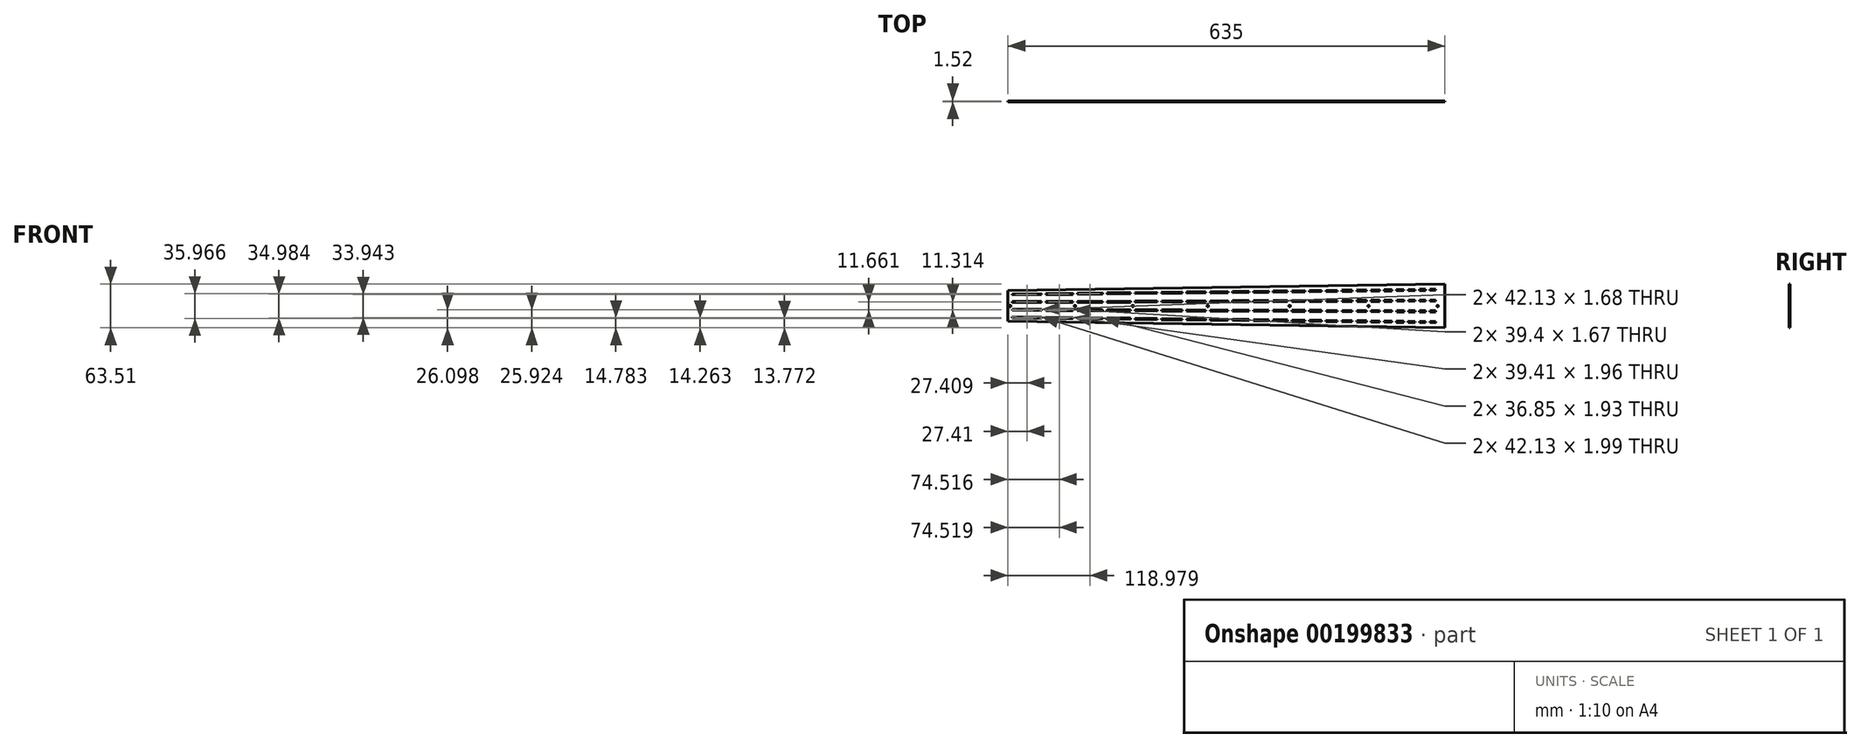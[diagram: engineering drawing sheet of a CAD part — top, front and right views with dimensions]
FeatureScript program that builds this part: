
annotation { "Feature Type Name" : "Feature", "Feature Type Description" : "" }
export const myFeature = defineFeature(function(context is Context, id is Id, definition is map)
    precondition{}
    {
        {
            var Q0;
            Q0=qCreatedBy(makeId("Front.planeOp"),FACE);
            var sketch = newSketch(context, id + "F0", { "sketchPlane" : qUnion([Q0])});
            skLineSegment(sketch, "E0", {"start": v(0, 5.56) * mm, "end": v(646.62, -1.59) * mm, "construction": true});
            skLineSegment(sketch, "E1", {"start": v(0, 6.32) * mm, "end": v(642.95, -0.78) * mm, "construction": true});
            skLineSegment(sketch, "E2", {"start": v(6.35, 5.49) * mm, "end": v(6.36, 6.25) * mm});
            skLineSegment(sketch, "E3", {"start": v(6.36, 6.25) * mm, "end": v(48.48, 5.78) * mm});
            skLineSegment(sketch, "E4", {"start": v(48.48, 5.78) * mm, "end": v(48.47, 5.02) * mm});
            skLineSegment(sketch, "E5", {"start": v(54.82, 4.95) * mm, "end": v(54.83, 5.71) * mm});
            skLineSegment(sketch, "E6", {"start": v(54.83, 5.71) * mm, "end": v(94.22, 5.28) * mm});
            skLineSegment(sketch, "E7", {"start": v(94.22, 5.28) * mm, "end": v(94.21, 4.52) * mm});
            skLineSegment(sketch, "E8", {"start": v(100.56, 4.45) * mm, "end": v(100.57, 5.2) * mm});
            skLineSegment(sketch, "E9", {"start": v(100.57, 5.2) * mm, "end": v(137.4, 4.8) * mm});
            skLineSegment(sketch, "E10", {"start": v(137.4, 4.8) * mm, "end": v(137.4, 4.04) * mm});
            skLineSegment(sketch, "E11", {"start": v(143.74, 3.97) * mm, "end": v(143.75, 4.73) * mm});
            skLineSegment(sketch, "E12", {"start": v(143.75, 4.73) * mm, "end": v(178.15, 4.35) * mm});
            skLineSegment(sketch, "E13", {"start": v(178.15, 4.35) * mm, "end": v(178.14, 3.59) * mm});
            skLineSegment(sketch, "E14", {"start": v(184.5, 3.52) * mm, "end": v(184.5, 4.28) * mm});
            skLineSegment(sketch, "E15", {"start": v(184.5, 4.28) * mm, "end": v(216.63, 3.93) * mm, "construction": true});
            skLineSegment(sketch, "E16", {"start": v(216.63, 3.93) * mm, "end": v(216.62, 3.16) * mm});
            skLineSegment(sketch, "E17", {"start": v(222.97, 3.1) * mm, "end": v(222.98, 3.85) * mm});
            skLineSegment(sketch, "E18", {"start": v(222.98, 3.85) * mm, "end": v(252.94, 3.52) * mm});
            skLineSegment(sketch, "E19", {"start": v(252.94, 3.52) * mm, "end": v(252.93, 2.76) * mm});
            skLineSegment(sketch, "E20", {"start": v(259.28, 2.7) * mm, "end": v(259.28, 3.45) * mm});
            skLineSegment(sketch, "E21", {"start": v(259.28, 3.45) * mm, "end": v(287.2, 3.15) * mm});
            skLineSegment(sketch, "E22", {"start": v(287.2, 3.15) * mm, "end": v(287.2, 2.38) * mm});
            skLineSegment(sketch, "E23", {"start": v(293.55, 2.31) * mm, "end": v(293.56, 3.08) * mm});
            skLineSegment(sketch, "E24", {"start": v(293.56, 3.08) * mm, "end": v(319.55, 2.79) * mm});
            skLineSegment(sketch, "E25", {"start": v(319.55, 2.79) * mm, "end": v(319.55, 2.03) * mm});
            skLineSegment(sketch, "E26", {"start": v(325.9, 1.96) * mm, "end": v(325.9, 2.72) * mm});
            skLineSegment(sketch, "E27", {"start": v(325.9, 2.72) * mm, "end": v(350.09, 2.45) * mm});
            skLineSegment(sketch, "E28", {"start": v(350.09, 2.45) * mm, "end": v(350.08, 1.69) * mm});
            skLineSegment(sketch, "E29", {"start": v(184.5, 4.28) * mm, "end": v(216.63, 3.93) * mm});
            skLineSegment(sketch, "E30", {"start": v(356.43, 1.62) * mm, "end": v(356.44, 2.38) * mm});
            skLineSegment(sketch, "E31", {"start": v(356.44, 2.38) * mm, "end": v(378.9, 2.13) * mm});
            skLineSegment(sketch, "E32", {"start": v(378.9, 2.13) * mm, "end": v(378.9, 1.37) * mm});
            skLineSegment(sketch, "E33", {"start": v(385.25, 1.3) * mm, "end": v(385.26, 2.06) * mm});
            skLineSegment(sketch, "E34", {"start": v(385.26, 2.06) * mm, "end": v(406.1, 1.83) * mm});
            skLineSegment(sketch, "E35", {"start": v(406.1, 1.83) * mm, "end": v(406.1, 1.07) * mm});
            skLineSegment(sketch, "E36", {"start": v(412.45, 1) * mm, "end": v(412.46, 1.76) * mm});
            skLineSegment(sketch, "E37", {"start": v(412.46, 1.76) * mm, "end": v(431.78, 1.55) * mm});
            skLineSegment(sketch, "E38", {"start": v(431.78, 1.55) * mm, "end": v(431.77, 0.79) * mm});
            skLineSegment(sketch, "E39", {"start": v(438.12, 0.72) * mm, "end": v(438.13, 1.48) * mm});
            skLineSegment(sketch, "E40", {"start": v(438.13, 1.48) * mm, "end": v(456.02, 1.28) * mm});
            skLineSegment(sketch, "E41", {"start": v(456.02, 1.28) * mm, "end": v(456, 0.52) * mm});
            skLineSegment(sketch, "E42", {"start": v(462.36, 0.45) * mm, "end": v(462.37, 1.21) * mm});
            skLineSegment(sketch, "E43", {"start": v(462.37, 1.21) * mm, "end": v(478.89, 1.03) * mm});
            skLineSegment(sketch, "E44", {"start": v(478.89, 1.03) * mm, "end": v(478.88, 0.27) * mm});
            skLineSegment(sketch, "E45", {"start": v(485.23, 0.2) * mm, "end": v(485.24, 0.96) * mm});
            skLineSegment(sketch, "E46", {"start": v(485.24, 0.96) * mm, "end": v(500.48, 0.79) * mm});
            skLineSegment(sketch, "E47", {"start": v(500.48, 0.79) * mm, "end": v(500.47, 0.03) * mm});
            skLineSegment(sketch, "E48", {"start": v(506.82, -0.04) * mm, "end": v(506.83, 0.72) * mm});
            skLineSegment(sketch, "E49", {"start": v(506.83, 0.72) * mm, "end": v(520.86, 0.56) * mm});
            skLineSegment(sketch, "E50", {"start": v(520.86, 0.56) * mm, "end": v(520.85, -0.2) * mm});
            skLineSegment(sketch, "E51", {"start": v(527.2, -0.27) * mm, "end": v(527.2, 0.5) * mm});
            skLineSegment(sketch, "E52", {"start": v(527.2, 0.5) * mm, "end": v(540.1, 0.35) * mm});
            skLineSegment(sketch, "E53", {"start": v(540.1, 0.35) * mm, "end": v(540.08, -0.41) * mm});
            skLineSegment(sketch, "E54", {"start": v(546.43, -0.48) * mm, "end": v(546.44, 0.28) * mm});
            skLineSegment(sketch, "E55", {"start": v(546.44, 0.28) * mm, "end": v(558.25, 0.15) * mm});
            skLineSegment(sketch, "E56", {"start": v(558.25, 0.15) * mm, "end": v(558.24, -0.61) * mm});
            skLineSegment(sketch, "E57", {"start": v(564.59, -0.68) * mm, "end": v(564.6, 0.08) * mm});
            skLineSegment(sketch, "E58", {"start": v(564.6, 0.08) * mm, "end": v(575.38, -0.04) * mm});
            skLineSegment(sketch, "E59", {"start": v(575.38, -0.04) * mm, "end": v(575.37, -0.8) * mm});
            skLineSegment(sketch, "E60", {"start": v(581.72, -0.87) * mm, "end": v(581.73, -0.1) * mm});
            skLineSegment(sketch, "E61", {"start": v(581.73, -0.1) * mm, "end": v(591.56, -0.22) * mm});
            skLineSegment(sketch, "E62", {"start": v(591.56, -0.22) * mm, "end": v(591.55, -0.98) * mm});
            skLineSegment(sketch, "E63", {"start": v(597.9, -1.05) * mm, "end": v(597.9, -0.29) * mm});
            skLineSegment(sketch, "E64", {"start": v(597.9, -0.29) * mm, "end": v(606.82, -0.39) * mm});
            skLineSegment(sketch, "E65", {"start": v(606.82, -0.39) * mm, "end": v(606.81, -1.15) * mm});
            skLineSegment(sketch, "E66", {"start": v(613.16, -1.22) * mm, "end": v(613.17, -0.46) * mm});
            skLineSegment(sketch, "E67", {"start": v(613.17, -0.46) * mm, "end": v(621.23, -0.54) * mm});
            skLineSegment(sketch, "E68", {"start": v(621.23, -0.54) * mm, "end": v(621.22, -1.3) * mm});
            skLineSegment(sketch, "E69.MirrorCS", {"start": v(184.5, 3.52) * mm, "end": v(184.48, 2.76) * mm});
            skLineSegment(sketch, "E70.MirrorCS", {"start": v(606.8, -1.9) * mm, "end": v(606.81, -1.15) * mm});
            skLineSegment(sketch, "E71.MirrorCS", {"start": v(222.97, 3.1) * mm, "end": v(222.96, 2.33) * mm});
            skLineSegment(sketch, "E72.MirrorCS", {"start": v(558.23, -1.37) * mm, "end": v(558.24, -0.61) * mm});
            skLineSegment(sketch, "E73.MirrorCS", {"start": v(216.6, 2.4) * mm, "end": v(216.62, 3.16) * mm});
            skLineSegment(sketch, "E74.MirrorCS", {"start": v(293.55, 2.31) * mm, "end": v(293.54, 1.55) * mm});
            skLineSegment(sketch, "E75.MirrorCS", {"start": v(94.2, 3.75) * mm, "end": v(94.21, 4.52) * mm});
            skLineSegment(sketch, "E76.MirrorCS", {"start": v(48.46, 4.26) * mm, "end": v(48.47, 5.02) * mm});
            skLineSegment(sketch, "E77.MirrorCS", {"start": v(613.16, -1.22) * mm, "end": v(613.15, -1.98) * mm});
            skLineSegment(sketch, "E78.MirrorCS", {"start": v(597.9, -1.05) * mm, "end": v(597.89, -1.81) * mm});
            skLineSegment(sketch, "E79.MirrorCS", {"start": v(325.9, 1.96) * mm, "end": v(325.89, 1.2) * mm});
            skLineSegment(sketch, "E80.MirrorCS", {"start": v(581.72, -0.87) * mm, "end": v(581.71, -1.63) * mm});
            skLineSegment(sketch, "E81.MirrorCS", {"start": v(478.87, -0.5) * mm, "end": v(478.88, 0.27) * mm});
            skLineSegment(sketch, "E82.MirrorCS", {"start": v(406.1, 0.3) * mm, "end": v(406.1, 1.07) * mm});
            skLineSegment(sketch, "E83.MirrorCS", {"start": v(591.54, -1.74) * mm, "end": v(591.55, -0.98) * mm});
            skLineSegment(sketch, "E84.MirrorCS", {"start": v(485.23, 0.2) * mm, "end": v(485.22, -0.57) * mm});
            skLineSegment(sketch, "E85.MirrorCS", {"start": v(581.71, -1.63) * mm, "end": v(591.54, -1.74) * mm});
            skLineSegment(sketch, "E86.MirrorCS", {"start": v(520.84, -0.96) * mm, "end": v(520.85, -0.2) * mm});
            skLineSegment(sketch, "E87.MirrorCS", {"start": v(319.54, 1.26) * mm, "end": v(319.55, 2.03) * mm});
            skLineSegment(sketch, "E88.MirrorCS", {"start": v(456, -0.24) * mm, "end": v(456, 0.52) * mm});
            skLineSegment(sketch, "E89.MirrorCS", {"start": v(564.59, -0.68) * mm, "end": v(564.58, -1.44) * mm});
            skLineSegment(sketch, "E90.MirrorCS", {"start": v(385.25, 1.3) * mm, "end": v(385.24, 0.54) * mm});
            skLineSegment(sketch, "E91.MirrorCS", {"start": v(378.89, 0.6) * mm, "end": v(378.9, 1.37) * mm});
            skLineSegment(sketch, "E92.MirrorCS", {"start": v(506.82, -0.04) * mm, "end": v(506.81, -0.8) * mm});
            skLineSegment(sketch, "E93.MirrorCS", {"start": v(597.89, -1.81) * mm, "end": v(606.8, -1.9) * mm});
            skLineSegment(sketch, "E94.MirrorCS", {"start": v(546.42, -1.24) * mm, "end": v(558.23, -1.37) * mm});
            skLineSegment(sketch, "E95.MirrorCS", {"start": v(143.74, 3.97) * mm, "end": v(143.74, 3.2) * mm});
            skLineSegment(sketch, "E96.MirrorCS", {"start": v(137.39, 3.28) * mm, "end": v(137.4, 4.04) * mm});
            skLineSegment(sketch, "E97.MirrorCS", {"start": v(100.56, 4.45) * mm, "end": v(100.56, 3.68) * mm});
            skLineSegment(sketch, "E98.MirrorCS", {"start": v(54.82, 4.95) * mm, "end": v(54.8, 4.19) * mm});
            skLineSegment(sketch, "E99.MirrorCS", {"start": v(6.35, 5.49) * mm, "end": v(6.34, 4.72) * mm});
            skLineSegment(sketch, "E100.MirrorCS", {"start": v(178.13, 2.83) * mm, "end": v(178.14, 3.59) * mm});
            skLineSegment(sketch, "E101.MirrorCS", {"start": v(431.77, 0.02) * mm, "end": v(431.77, 0.79) * mm});
            skLineSegment(sketch, "E102.MirrorCS", {"start": v(546.43, -0.48) * mm, "end": v(546.42, -1.24) * mm});
            skLineSegment(sketch, "E103.MirrorCS", {"start": v(500.46, -0.73) * mm, "end": v(500.47, 0.03) * mm});
            skLineSegment(sketch, "E104.MirrorCS", {"start": v(287.2, 1.62) * mm, "end": v(287.2, 2.38) * mm});
            skLineSegment(sketch, "E105.MirrorCS", {"start": v(564.58, -1.44) * mm, "end": v(575.36, -1.56) * mm});
            skLineSegment(sketch, "E106.MirrorCS", {"start": v(252.92, 2) * mm, "end": v(252.93, 2.76) * mm});
            skLineSegment(sketch, "E107.MirrorCS", {"start": v(613.15, -1.98) * mm, "end": v(621.21, -2.07) * mm});
            skLineSegment(sketch, "E108.MirrorCS", {"start": v(527.2, -0.27) * mm, "end": v(527.19, -1.03) * mm});
            skLineSegment(sketch, "E109.MirrorCS", {"start": v(350.07, 0.93) * mm, "end": v(350.08, 1.69) * mm});
            skLineSegment(sketch, "E110.MirrorCS", {"start": v(412.45, 1) * mm, "end": v(412.44, 0.24) * mm});
            skLineSegment(sketch, "E111.MirrorCS", {"start": v(575.36, -1.56) * mm, "end": v(575.37, -0.8) * mm});
            skLineSegment(sketch, "E112.MirrorCS", {"start": v(259.28, 2.7) * mm, "end": v(259.27, 1.93) * mm});
            skLineSegment(sketch, "E113.MirrorCS", {"start": v(621.21, -2.07) * mm, "end": v(621.22, -1.3) * mm});
            skLineSegment(sketch, "E114.MirrorCS", {"start": v(356.43, 1.62) * mm, "end": v(356.42, 0.86) * mm});
            skLineSegment(sketch, "E115.MirrorCS", {"start": v(506.81, -0.8) * mm, "end": v(520.84, -0.96) * mm});
            skLineSegment(sketch, "E116.MirrorCS", {"start": v(438.12, 0.72) * mm, "end": v(438.11, -0.05) * mm});
            skLineSegment(sketch, "E117.MirrorCS", {"start": v(184.48, 2.76) * mm, "end": v(216.6, 2.4) * mm, "construction": true});
            skLineSegment(sketch, "E118.MirrorCS", {"start": v(462.36, 0.45) * mm, "end": v(462.35, -0.31) * mm});
            skLineSegment(sketch, "E119.MirrorCS", {"start": v(540.07, -1.17) * mm, "end": v(540.08, -0.41) * mm});
            skLineSegment(sketch, "E120.MirrorCS", {"start": v(527.19, -1.03) * mm, "end": v(540.07, -1.17) * mm});
            skLineSegment(sketch, "E121.MirrorCS", {"start": v(222.96, 2.33) * mm, "end": v(252.92, 2) * mm});
            skLineSegment(sketch, "E122.MirrorCS", {"start": v(385.24, 0.54) * mm, "end": v(406.1, 0.3) * mm});
            skLineSegment(sketch, "E123.MirrorCS", {"start": v(293.54, 1.55) * mm, "end": v(319.54, 1.26) * mm});
            skLineSegment(sketch, "E124.MirrorCS", {"start": v(438.11, -0.05) * mm, "end": v(456, -0.24) * mm});
            skLineSegment(sketch, "E125.MirrorCS", {"start": v(143.74, 3.2) * mm, "end": v(178.13, 2.83) * mm});
            skLineSegment(sketch, "E126.MirrorCS", {"start": v(54.8, 4.19) * mm, "end": v(94.2, 3.75) * mm});
            skLineSegment(sketch, "E127.MirrorCS", {"start": v(6.34, 4.72) * mm, "end": v(48.46, 4.26) * mm});
            skLineSegment(sketch, "E128.MirrorCS", {"start": v(356.42, 0.86) * mm, "end": v(378.89, 0.6) * mm});
            skLineSegment(sketch, "E129.MirrorCS", {"start": v(259.27, 1.93) * mm, "end": v(287.2, 1.62) * mm});
            skLineSegment(sketch, "E130.MirrorCS", {"start": v(485.22, -0.57) * mm, "end": v(500.46, -0.73) * mm});
            skLineSegment(sketch, "E131.MirrorCS", {"start": v(412.44, 0.24) * mm, "end": v(431.77, 0.02) * mm});
            skLineSegment(sketch, "E132.MirrorCS", {"start": v(184.48, 2.76) * mm, "end": v(216.6, 2.4) * mm});
            skLineSegment(sketch, "E133.MirrorCS", {"start": v(462.35, -0.31) * mm, "end": v(478.87, -0.5) * mm});
            skLineSegment(sketch, "E134.MirrorCS", {"start": v(325.89, 1.2) * mm, "end": v(350.07, 0.93) * mm});
            skLineSegment(sketch, "E135.MirrorCS", {"start": v(100.56, 3.68) * mm, "end": v(137.39, 3.28) * mm});
            skLineSegment(sketch, "E136", {"start": v(-33.04, 0) * mm, "end": v(118.54, 0) * mm, "construction": true});
            skLineSegment(sketch, "E137", {"start": v(0, 16.67) * mm, "end": v(646.66, 14.29) * mm, "construction": true});
            skLineSegment(sketch, "E138", {"start": v(0, 17.43) * mm, "end": v(642.97, 15.06) * mm, "construction": true});
            skLineSegment(sketch, "E139", {"start": v(6.35, 16.65) * mm, "end": v(6.35, 17.4) * mm});
            skLineSegment(sketch, "E140", {"start": v(6.35, 17.4) * mm, "end": v(48.47, 17.25) * mm});
            skLineSegment(sketch, "E141", {"start": v(48.47, 17.25) * mm, "end": v(48.47, 16.5) * mm});
            skLineSegment(sketch, "E142", {"start": v(54.82, 16.47) * mm, "end": v(54.82, 17.23) * mm});
            skLineSegment(sketch, "E143", {"start": v(54.82, 17.23) * mm, "end": v(94.22, 17.08) * mm});
            skLineSegment(sketch, "E144", {"start": v(94.22, 17.08) * mm, "end": v(94.22, 16.32) * mm});
            skLineSegment(sketch, "E145", {"start": v(100.57, 16.3) * mm, "end": v(100.57, 17.06) * mm});
            skLineSegment(sketch, "E146", {"start": v(100.57, 17.06) * mm, "end": v(137.4, 16.92) * mm});
            skLineSegment(sketch, "E147", {"start": v(137.4, 16.92) * mm, "end": v(137.4, 16.16) * mm});
            skLineSegment(sketch, "E148", {"start": v(143.75, 16.14) * mm, "end": v(143.75, 16.9) * mm});
            skLineSegment(sketch, "E149", {"start": v(143.75, 16.9) * mm, "end": v(178.15, 16.77) * mm});
            skLineSegment(sketch, "E150", {"start": v(178.15, 16.77) * mm, "end": v(178.15, 16.01) * mm});
            skLineSegment(sketch, "E151", {"start": v(184.5, 15.99) * mm, "end": v(184.5, 16.75) * mm});
            skLineSegment(sketch, "E152", {"start": v(184.5, 16.75) * mm, "end": v(216.63, 16.63) * mm, "construction": true});
            skLineSegment(sketch, "E153", {"start": v(216.63, 16.63) * mm, "end": v(216.63, 15.87) * mm});
            skLineSegment(sketch, "E154", {"start": v(222.98, 15.85) * mm, "end": v(222.98, 16.6) * mm});
            skLineSegment(sketch, "E155", {"start": v(222.98, 16.6) * mm, "end": v(252.94, 16.5) * mm});
            skLineSegment(sketch, "E156", {"start": v(252.94, 16.5) * mm, "end": v(252.94, 15.74) * mm});
            skLineSegment(sketch, "E157", {"start": v(259.3, 15.71) * mm, "end": v(259.3, 16.48) * mm});
            skLineSegment(sketch, "E158", {"start": v(259.3, 16.48) * mm, "end": v(287.22, 16.37) * mm});
            skLineSegment(sketch, "E159", {"start": v(287.22, 16.37) * mm, "end": v(287.21, 15.61) * mm});
            skLineSegment(sketch, "E160", {"start": v(293.56, 15.59) * mm, "end": v(293.57, 16.35) * mm});
            skLineSegment(sketch, "E161", {"start": v(293.57, 16.35) * mm, "end": v(319.57, 16.25) * mm});
            skLineSegment(sketch, "E162", {"start": v(319.57, 16.25) * mm, "end": v(319.56, 15.5) * mm});
            skLineSegment(sketch, "E163", {"start": v(325.91, 15.47) * mm, "end": v(325.92, 16.23) * mm});
            skLineSegment(sketch, "E164", {"start": v(325.92, 16.23) * mm, "end": v(350.1, 16.14) * mm});
            skLineSegment(sketch, "E165", {"start": v(350.1, 16.14) * mm, "end": v(350.1, 15.38) * mm});
            skLineSegment(sketch, "E166", {"start": v(184.5, 16.75) * mm, "end": v(216.63, 16.63) * mm});
            skLineSegment(sketch, "E167", {"start": v(356.45, 15.36) * mm, "end": v(356.45, 16.12) * mm});
            skLineSegment(sketch, "E168", {"start": v(356.45, 16.12) * mm, "end": v(378.92, 16.04) * mm});
            skLineSegment(sketch, "E169", {"start": v(378.92, 16.04) * mm, "end": v(378.92, 15.27) * mm});
            skLineSegment(sketch, "E170", {"start": v(385.27, 15.25) * mm, "end": v(385.27, 16.01) * mm});
            skLineSegment(sketch, "E171", {"start": v(385.27, 16.01) * mm, "end": v(406.12, 15.94) * mm});
            skLineSegment(sketch, "E172", {"start": v(406.12, 15.94) * mm, "end": v(406.12, 15.17) * mm});
            skLineSegment(sketch, "E173", {"start": v(412.47, 15.15) * mm, "end": v(412.47, 15.91) * mm});
            skLineSegment(sketch, "E174", {"start": v(412.47, 15.91) * mm, "end": v(431.8, 15.84) * mm});
            skLineSegment(sketch, "E175", {"start": v(431.8, 15.84) * mm, "end": v(431.8, 15.08) * mm});
            skLineSegment(sketch, "E176", {"start": v(438.15, 15.06) * mm, "end": v(438.15, 15.82) * mm});
            skLineSegment(sketch, "E177", {"start": v(438.15, 15.82) * mm, "end": v(456.03, 15.75) * mm});
            skLineSegment(sketch, "E178", {"start": v(456.03, 15.75) * mm, "end": v(456.03, 14.99) * mm});
            skLineSegment(sketch, "E179", {"start": v(462.38, 14.97) * mm, "end": v(462.38, 15.73) * mm});
            skLineSegment(sketch, "E180", {"start": v(462.38, 15.73) * mm, "end": v(478.9, 15.67) * mm});
            skLineSegment(sketch, "E181", {"start": v(478.9, 15.67) * mm, "end": v(478.9, 14.9) * mm});
            skLineSegment(sketch, "E182", {"start": v(485.26, 14.88) * mm, "end": v(485.26, 15.64) * mm});
            skLineSegment(sketch, "E183", {"start": v(485.26, 15.64) * mm, "end": v(500.5, 15.59) * mm});
            skLineSegment(sketch, "E184", {"start": v(500.5, 15.59) * mm, "end": v(500.5, 14.83) * mm});
            skLineSegment(sketch, "E185", {"start": v(506.85, 14.8) * mm, "end": v(506.85, 15.56) * mm});
            skLineSegment(sketch, "E186", {"start": v(506.85, 15.56) * mm, "end": v(520.88, 15.51) * mm});
            skLineSegment(sketch, "E187", {"start": v(520.88, 15.51) * mm, "end": v(520.88, 14.75) * mm});
            skLineSegment(sketch, "E188", {"start": v(527.23, 14.73) * mm, "end": v(527.23, 15.49) * mm});
            skLineSegment(sketch, "E189", {"start": v(527.23, 15.49) * mm, "end": v(540.11, 15.44) * mm});
            skLineSegment(sketch, "E190", {"start": v(540.11, 15.44) * mm, "end": v(540.11, 14.68) * mm});
            skLineSegment(sketch, "E191", {"start": v(546.46, 14.66) * mm, "end": v(546.46, 15.42) * mm});
            skLineSegment(sketch, "E192", {"start": v(546.46, 15.42) * mm, "end": v(558.27, 15.37) * mm});
            skLineSegment(sketch, "E193", {"start": v(558.27, 15.37) * mm, "end": v(558.27, 14.61) * mm});
            skLineSegment(sketch, "E194", {"start": v(564.62, 14.59) * mm, "end": v(564.62, 15.35) * mm});
            skLineSegment(sketch, "E195", {"start": v(564.62, 15.35) * mm, "end": v(575.4, 15.31) * mm});
            skLineSegment(sketch, "E196", {"start": v(575.4, 15.31) * mm, "end": v(575.4, 14.55) * mm});
            skLineSegment(sketch, "E197", {"start": v(581.75, 14.53) * mm, "end": v(581.76, 15.29) * mm});
            skLineSegment(sketch, "E198", {"start": v(581.76, 15.29) * mm, "end": v(591.58, 15.25) * mm});
            skLineSegment(sketch, "E199", {"start": v(591.58, 15.25) * mm, "end": v(591.58, 14.5) * mm});
            skLineSegment(sketch, "E200", {"start": v(597.93, 14.47) * mm, "end": v(597.93, 15.23) * mm});
            skLineSegment(sketch, "E201", {"start": v(597.93, 15.23) * mm, "end": v(606.85, 15.2) * mm});
            skLineSegment(sketch, "E202", {"start": v(606.85, 15.2) * mm, "end": v(606.85, 14.43) * mm});
            skLineSegment(sketch, "E203", {"start": v(613.2, 14.41) * mm, "end": v(613.2, 15.17) * mm});
            skLineSegment(sketch, "E204", {"start": v(613.2, 15.17) * mm, "end": v(621.26, 15.14) * mm});
            skLineSegment(sketch, "E205", {"start": v(621.26, 15.14) * mm, "end": v(621.26, 14.38) * mm});
            skLineSegment(sketch, "E206.MirrorCS", {"start": v(184.5, 15.99) * mm, "end": v(184.5, 15.23) * mm});
            skLineSegment(sketch, "E207.MirrorCS", {"start": v(606.84, 13.67) * mm, "end": v(606.85, 14.43) * mm});
            skLineSegment(sketch, "E208.MirrorCS", {"start": v(222.98, 15.85) * mm, "end": v(222.98, 15.09) * mm});
            skLineSegment(sketch, "E209.MirrorCS", {"start": v(558.27, 13.85) * mm, "end": v(558.27, 14.61) * mm});
            skLineSegment(sketch, "E210.MirrorCS", {"start": v(216.63, 15.1) * mm, "end": v(216.63, 15.87) * mm});
            skLineSegment(sketch, "E211.MirrorCS", {"start": v(293.56, 15.59) * mm, "end": v(293.56, 14.83) * mm});
            skLineSegment(sketch, "E212.MirrorCS", {"start": v(94.22, 15.56) * mm, "end": v(94.22, 16.32) * mm});
            skLineSegment(sketch, "E213.MirrorCS", {"start": v(48.47, 15.73) * mm, "end": v(48.47, 16.5) * mm});
            skLineSegment(sketch, "E214.MirrorCS", {"start": v(613.2, 14.41) * mm, "end": v(613.2, 13.65) * mm});
            skLineSegment(sketch, "E215.MirrorCS", {"start": v(597.93, 14.47) * mm, "end": v(597.93, 13.7) * mm});
            skLineSegment(sketch, "E216.MirrorCS", {"start": v(325.91, 15.47) * mm, "end": v(325.91, 14.7) * mm});
            skLineSegment(sketch, "E217.MirrorCS", {"start": v(581.75, 14.53) * mm, "end": v(581.75, 13.76) * mm});
            skLineSegment(sketch, "E218.MirrorCS", {"start": v(478.9, 14.14) * mm, "end": v(478.9, 14.9) * mm});
            skLineSegment(sketch, "E219.MirrorCS", {"start": v(406.12, 14.41) * mm, "end": v(406.12, 15.17) * mm});
            skLineSegment(sketch, "E220.MirrorCS", {"start": v(591.58, 13.73) * mm, "end": v(591.58, 14.5) * mm});
            skLineSegment(sketch, "E221.MirrorCS", {"start": v(485.26, 14.88) * mm, "end": v(485.25, 14.12) * mm});
            skLineSegment(sketch, "E222.MirrorCS", {"start": v(581.75, 13.76) * mm, "end": v(591.58, 13.73) * mm});
            skLineSegment(sketch, "E223.MirrorCS", {"start": v(520.87, 13.99) * mm, "end": v(520.88, 14.75) * mm});
            skLineSegment(sketch, "E224.MirrorCS", {"start": v(319.56, 14.73) * mm, "end": v(319.56, 15.5) * mm});
            skLineSegment(sketch, "E225.MirrorCS", {"start": v(456.03, 14.23) * mm, "end": v(456.03, 14.99) * mm});
            skLineSegment(sketch, "E226.MirrorCS", {"start": v(564.62, 14.59) * mm, "end": v(564.61, 13.83) * mm});
            skLineSegment(sketch, "E227.MirrorCS", {"start": v(385.27, 15.25) * mm, "end": v(385.27, 14.49) * mm});
            skLineSegment(sketch, "E228.MirrorCS", {"start": v(378.92, 14.51) * mm, "end": v(378.92, 15.27) * mm});
            skLineSegment(sketch, "E229.MirrorCS", {"start": v(506.85, 14.8) * mm, "end": v(506.84, 14.04) * mm});
            skLineSegment(sketch, "E230.MirrorCS", {"start": v(597.93, 13.7) * mm, "end": v(606.84, 13.67) * mm});
            skLineSegment(sketch, "E231.MirrorCS", {"start": v(546.46, 13.9) * mm, "end": v(558.27, 13.85) * mm});
            skLineSegment(sketch, "E232.MirrorCS", {"start": v(143.75, 16.14) * mm, "end": v(143.75, 15.38) * mm});
            skLineSegment(sketch, "E233.MirrorCS", {"start": v(137.4, 15.4) * mm, "end": v(137.4, 16.16) * mm});
            skLineSegment(sketch, "E234.MirrorCS", {"start": v(100.57, 16.3) * mm, "end": v(100.57, 15.54) * mm});
            skLineSegment(sketch, "E235.MirrorCS", {"start": v(54.82, 16.47) * mm, "end": v(54.82, 15.7) * mm});
            skLineSegment(sketch, "E236.MirrorCS", {"start": v(6.35, 16.65) * mm, "end": v(6.35, 15.88) * mm});
            skLineSegment(sketch, "E237.MirrorCS", {"start": v(178.15, 15.25) * mm, "end": v(178.15, 16.01) * mm});
            skLineSegment(sketch, "E238.MirrorCS", {"start": v(431.8, 14.32) * mm, "end": v(431.8, 15.08) * mm});
            skLineSegment(sketch, "E239.MirrorCS", {"start": v(546.46, 14.66) * mm, "end": v(546.46, 13.9) * mm});
            skLineSegment(sketch, "E240.MirrorCS", {"start": v(500.5, 14.06) * mm, "end": v(500.5, 14.83) * mm});
            skLineSegment(sketch, "E241.MirrorCS", {"start": v(287.21, 14.85) * mm, "end": v(287.21, 15.61) * mm});
            skLineSegment(sketch, "E242.MirrorCS", {"start": v(564.61, 13.83) * mm, "end": v(575.4, 13.79) * mm});
            skLineSegment(sketch, "E243.MirrorCS", {"start": v(252.94, 14.98) * mm, "end": v(252.94, 15.74) * mm});
            skLineSegment(sketch, "E244.MirrorCS", {"start": v(613.2, 13.65) * mm, "end": v(621.25, 13.62) * mm});
            skLineSegment(sketch, "E245.MirrorCS", {"start": v(527.23, 14.73) * mm, "end": v(527.22, 13.97) * mm});
            skLineSegment(sketch, "E246.MirrorCS", {"start": v(350.1, 14.62) * mm, "end": v(350.1, 15.38) * mm});
            skLineSegment(sketch, "E247.MirrorCS", {"start": v(412.47, 15.15) * mm, "end": v(412.47, 14.39) * mm});
            skLineSegment(sketch, "E248.MirrorCS", {"start": v(575.4, 13.79) * mm, "end": v(575.4, 14.55) * mm});
            skLineSegment(sketch, "E249.MirrorCS", {"start": v(259.3, 15.71) * mm, "end": v(259.29, 14.95) * mm});
            skLineSegment(sketch, "E250.MirrorCS", {"start": v(621.25, 13.62) * mm, "end": v(621.26, 14.38) * mm});
            skLineSegment(sketch, "E251.MirrorCS", {"start": v(356.45, 15.36) * mm, "end": v(356.44, 14.6) * mm});
            skLineSegment(sketch, "E252.MirrorCS", {"start": v(506.84, 14.04) * mm, "end": v(520.87, 13.99) * mm});
            skLineSegment(sketch, "E253.MirrorCS", {"start": v(438.15, 15.06) * mm, "end": v(438.14, 14.3) * mm});
            skLineSegment(sketch, "E254.MirrorCS", {"start": v(184.5, 15.23) * mm, "end": v(216.63, 15.1) * mm, "construction": true});
            skLineSegment(sketch, "E255.MirrorCS", {"start": v(462.38, 14.97) * mm, "end": v(462.38, 14.2) * mm});
            skLineSegment(sketch, "E256.MirrorCS", {"start": v(540.1, 13.92) * mm, "end": v(540.11, 14.68) * mm});
            skLineSegment(sketch, "E257.MirrorCS", {"start": v(527.22, 13.97) * mm, "end": v(540.1, 13.92) * mm});
            skLineSegment(sketch, "E258.MirrorCS", {"start": v(222.98, 15.09) * mm, "end": v(252.94, 14.98) * mm});
            skLineSegment(sketch, "E259.MirrorCS", {"start": v(385.27, 14.49) * mm, "end": v(406.12, 14.41) * mm});
            skLineSegment(sketch, "E260.MirrorCS", {"start": v(293.56, 14.83) * mm, "end": v(319.56, 14.73) * mm});
            skLineSegment(sketch, "E261.MirrorCS", {"start": v(438.14, 14.3) * mm, "end": v(456.03, 14.23) * mm});
            skLineSegment(sketch, "E262.MirrorCS", {"start": v(143.75, 15.38) * mm, "end": v(178.15, 15.25) * mm});
            skLineSegment(sketch, "E263.MirrorCS", {"start": v(54.82, 15.7) * mm, "end": v(94.22, 15.56) * mm});
            skLineSegment(sketch, "E264.MirrorCS", {"start": v(6.35, 15.88) * mm, "end": v(48.47, 15.73) * mm});
            skLineSegment(sketch, "E265.MirrorCS", {"start": v(356.44, 14.6) * mm, "end": v(378.92, 14.51) * mm});
            skLineSegment(sketch, "E266.MirrorCS", {"start": v(259.29, 14.95) * mm, "end": v(287.21, 14.85) * mm});
            skLineSegment(sketch, "E267.MirrorCS", {"start": v(485.25, 14.12) * mm, "end": v(500.5, 14.06) * mm});
            skLineSegment(sketch, "E268.MirrorCS", {"start": v(412.47, 14.39) * mm, "end": v(431.8, 14.32) * mm});
            skLineSegment(sketch, "E269.MirrorCS", {"start": v(184.5, 15.23) * mm, "end": v(216.63, 15.1) * mm});
            skLineSegment(sketch, "E270.MirrorCS", {"start": v(462.38, 14.2) * mm, "end": v(478.9, 14.14) * mm});
            skLineSegment(sketch, "E271.MirrorCS", {"start": v(325.91, 14.7) * mm, "end": v(350.1, 14.62) * mm});
            skLineSegment(sketch, "E272.MirrorCS", {"start": v(100.57, 15.54) * mm, "end": v(137.4, 15.4) * mm});
            skLineSegment(sketch, "E273", {"start": v(0, 27.78) * mm, "end": v(646.66, 30.16) * mm, "construction": true});
            skLineSegment(sketch, "E274", {"start": v(0, 28.54) * mm, "end": v(642.97, 30.91) * mm, "construction": true});
            skLineSegment(sketch, "E275", {"start": v(6.35, 27.8) * mm, "end": v(6.35, 28.57) * mm});
            skLineSegment(sketch, "E276", {"start": v(6.35, 28.57) * mm, "end": v(48.47, 28.72) * mm});
            skLineSegment(sketch, "E277", {"start": v(48.47, 28.72) * mm, "end": v(48.47, 27.96) * mm});
            skLineSegment(sketch, "E278", {"start": v(54.82, 27.98) * mm, "end": v(54.82, 28.75) * mm});
            skLineSegment(sketch, "E279", {"start": v(54.82, 28.75) * mm, "end": v(94.22, 28.9) * mm});
            skLineSegment(sketch, "E280", {"start": v(94.22, 28.9) * mm, "end": v(94.22, 28.13) * mm});
            skLineSegment(sketch, "E281", {"start": v(100.57, 28.15) * mm, "end": v(100.57, 28.91) * mm});
            skLineSegment(sketch, "E282", {"start": v(100.57, 28.91) * mm, "end": v(137.4, 29.05) * mm});
            skLineSegment(sketch, "E283", {"start": v(137.4, 29.05) * mm, "end": v(137.4, 28.29) * mm});
            skLineSegment(sketch, "E284", {"start": v(143.75, 28.31) * mm, "end": v(143.75, 29.07) * mm});
            skLineSegment(sketch, "E285", {"start": v(143.75, 29.07) * mm, "end": v(178.15, 29.2) * mm});
            skLineSegment(sketch, "E286", {"start": v(178.15, 29.2) * mm, "end": v(178.15, 28.44) * mm});
            skLineSegment(sketch, "E287", {"start": v(184.5, 28.46) * mm, "end": v(184.5, 29.22) * mm});
            skLineSegment(sketch, "E288", {"start": v(184.5, 29.22) * mm, "end": v(216.63, 29.34) * mm, "construction": true});
            skLineSegment(sketch, "E289", {"start": v(216.63, 29.34) * mm, "end": v(216.63, 28.58) * mm});
            skLineSegment(sketch, "E290", {"start": v(222.98, 28.6) * mm, "end": v(222.98, 29.36) * mm});
            skLineSegment(sketch, "E291", {"start": v(222.98, 29.36) * mm, "end": v(252.94, 29.47) * mm});
            skLineSegment(sketch, "E292", {"start": v(252.94, 29.47) * mm, "end": v(252.94, 28.71) * mm});
            skLineSegment(sketch, "E293", {"start": v(259.3, 28.74) * mm, "end": v(259.29, 29.5) * mm});
            skLineSegment(sketch, "E294", {"start": v(259.29, 29.5) * mm, "end": v(287.21, 29.6) * mm});
            skLineSegment(sketch, "E295", {"start": v(287.21, 29.6) * mm, "end": v(287.21, 28.84) * mm});
            skLineSegment(sketch, "E296", {"start": v(293.56, 28.86) * mm, "end": v(293.56, 29.62) * mm});
            skLineSegment(sketch, "E297", {"start": v(293.56, 29.62) * mm, "end": v(319.56, 29.72) * mm});
            skLineSegment(sketch, "E298", {"start": v(319.56, 29.72) * mm, "end": v(319.56, 28.96) * mm});
            skLineSegment(sketch, "E299", {"start": v(325.91, 28.98) * mm, "end": v(325.91, 29.74) * mm});
            skLineSegment(sketch, "E300", {"start": v(325.91, 29.74) * mm, "end": v(350.1, 29.83) * mm});
            skLineSegment(sketch, "E301", {"start": v(350.1, 29.83) * mm, "end": v(350.1, 29.07) * mm});
            skLineSegment(sketch, "E302", {"start": v(184.5, 29.22) * mm, "end": v(216.63, 29.34) * mm});
            skLineSegment(sketch, "E303", {"start": v(356.45, 29.1) * mm, "end": v(356.44, 29.86) * mm});
            skLineSegment(sketch, "E304", {"start": v(356.44, 29.86) * mm, "end": v(378.92, 29.94) * mm});
            skLineSegment(sketch, "E305", {"start": v(378.92, 29.94) * mm, "end": v(378.92, 29.18) * mm});
            skLineSegment(sketch, "E306", {"start": v(385.27, 29.2) * mm, "end": v(385.27, 29.96) * mm});
            skLineSegment(sketch, "E307", {"start": v(385.27, 29.96) * mm, "end": v(406.12, 30.04) * mm});
            skLineSegment(sketch, "E308", {"start": v(406.12, 30.04) * mm, "end": v(406.12, 29.28) * mm});
            skLineSegment(sketch, "E309", {"start": v(412.47, 29.3) * mm, "end": v(412.47, 30.06) * mm});
            skLineSegment(sketch, "E310", {"start": v(412.47, 30.06) * mm, "end": v(431.8, 30.13) * mm});
            skLineSegment(sketch, "E311", {"start": v(431.8, 30.13) * mm, "end": v(431.8, 29.37) * mm});
            skLineSegment(sketch, "E312", {"start": v(438.15, 29.4) * mm, "end": v(438.14, 30.16) * mm});
            skLineSegment(sketch, "E313", {"start": v(438.14, 30.16) * mm, "end": v(456.03, 30.22) * mm});
            skLineSegment(sketch, "E314", {"start": v(456.03, 30.22) * mm, "end": v(456.03, 29.46) * mm});
            skLineSegment(sketch, "E315", {"start": v(462.38, 29.48) * mm, "end": v(462.38, 30.25) * mm});
            skLineSegment(sketch, "E316", {"start": v(462.38, 30.25) * mm, "end": v(478.9, 30.3) * mm});
            skLineSegment(sketch, "E317", {"start": v(478.9, 30.3) * mm, "end": v(478.9, 29.54) * mm});
            skLineSegment(sketch, "E318", {"start": v(485.26, 29.57) * mm, "end": v(485.25, 30.33) * mm});
            skLineSegment(sketch, "E319", {"start": v(485.25, 30.33) * mm, "end": v(500.5, 30.39) * mm});
            skLineSegment(sketch, "E320", {"start": v(500.5, 30.39) * mm, "end": v(500.5, 29.62) * mm});
            skLineSegment(sketch, "E321", {"start": v(506.85, 29.65) * mm, "end": v(506.84, 30.4) * mm});
            skLineSegment(sketch, "E322", {"start": v(506.84, 30.4) * mm, "end": v(520.87, 30.46) * mm});
            skLineSegment(sketch, "E323", {"start": v(520.87, 30.46) * mm, "end": v(520.88, 29.7) * mm});
            skLineSegment(sketch, "E324", {"start": v(527.23, 29.72) * mm, "end": v(527.22, 30.48) * mm});
            skLineSegment(sketch, "E325", {"start": v(527.22, 30.48) * mm, "end": v(540.1, 30.53) * mm});
            skLineSegment(sketch, "E326", {"start": v(540.1, 30.53) * mm, "end": v(540.11, 29.77) * mm});
            skLineSegment(sketch, "E327", {"start": v(546.46, 29.8) * mm, "end": v(546.46, 30.56) * mm});
            skLineSegment(sketch, "E328", {"start": v(546.46, 30.56) * mm, "end": v(558.27, 30.6) * mm});
            skLineSegment(sketch, "E329", {"start": v(558.27, 30.6) * mm, "end": v(558.27, 29.84) * mm});
            skLineSegment(sketch, "E330", {"start": v(564.62, 29.86) * mm, "end": v(564.61, 30.62) * mm});
            skLineSegment(sketch, "E331", {"start": v(564.61, 30.62) * mm, "end": v(575.4, 30.66) * mm});
            skLineSegment(sketch, "E332", {"start": v(575.4, 30.66) * mm, "end": v(575.4, 29.9) * mm});
            skLineSegment(sketch, "E333", {"start": v(581.75, 29.92) * mm, "end": v(581.75, 30.69) * mm});
            skLineSegment(sketch, "E334", {"start": v(581.75, 30.69) * mm, "end": v(591.58, 30.72) * mm});
            skLineSegment(sketch, "E335", {"start": v(591.58, 30.72) * mm, "end": v(591.58, 29.96) * mm});
            skLineSegment(sketch, "E336", {"start": v(597.93, 29.98) * mm, "end": v(597.93, 30.75) * mm});
            skLineSegment(sketch, "E337", {"start": v(597.93, 30.75) * mm, "end": v(606.84, 30.78) * mm});
            skLineSegment(sketch, "E338", {"start": v(606.84, 30.78) * mm, "end": v(606.85, 30.02) * mm});
            skLineSegment(sketch, "E339", {"start": v(613.2, 30.04) * mm, "end": v(613.2, 30.8) * mm});
            skLineSegment(sketch, "E340", {"start": v(613.2, 30.8) * mm, "end": v(621.25, 30.83) * mm});
            skLineSegment(sketch, "E341", {"start": v(621.25, 30.83) * mm, "end": v(621.26, 30.07) * mm});
            skLineSegment(sketch, "E342.MirrorCS", {"start": v(184.5, 28.46) * mm, "end": v(184.5, 27.7) * mm});
            skLineSegment(sketch, "E343.MirrorCS", {"start": v(606.85, 29.25) * mm, "end": v(606.85, 30.02) * mm});
            skLineSegment(sketch, "E344.MirrorCS", {"start": v(222.98, 28.6) * mm, "end": v(222.98, 27.84) * mm});
            skLineSegment(sketch, "E345.MirrorCS", {"start": v(558.27, 29.08) * mm, "end": v(558.27, 29.84) * mm});
            skLineSegment(sketch, "E346.MirrorCS", {"start": v(216.63, 27.82) * mm, "end": v(216.63, 28.58) * mm});
            skLineSegment(sketch, "E347.MirrorCS", {"start": v(293.56, 28.86) * mm, "end": v(293.57, 28.1) * mm});
            skLineSegment(sketch, "E348.MirrorCS", {"start": v(94.22, 27.37) * mm, "end": v(94.22, 28.13) * mm});
            skLineSegment(sketch, "E349.MirrorCS", {"start": v(48.47, 27.2) * mm, "end": v(48.47, 27.96) * mm});
            skLineSegment(sketch, "E350.MirrorCS", {"start": v(613.2, 30.04) * mm, "end": v(613.2, 29.28) * mm});
            skLineSegment(sketch, "E351.MirrorCS", {"start": v(597.93, 29.98) * mm, "end": v(597.93, 29.22) * mm});
            skLineSegment(sketch, "E352.MirrorCS", {"start": v(325.91, 28.98) * mm, "end": v(325.92, 28.22) * mm});
            skLineSegment(sketch, "E353.MirrorCS", {"start": v(581.75, 29.92) * mm, "end": v(581.76, 29.16) * mm});
            skLineSegment(sketch, "E354.MirrorCS", {"start": v(478.9, 28.78) * mm, "end": v(478.9, 29.54) * mm});
            skLineSegment(sketch, "E355.MirrorCS", {"start": v(406.12, 28.51) * mm, "end": v(406.12, 29.28) * mm});
            skLineSegment(sketch, "E356.MirrorCS", {"start": v(591.58, 29.2) * mm, "end": v(591.58, 29.96) * mm});
            skLineSegment(sketch, "E357.MirrorCS", {"start": v(485.26, 29.57) * mm, "end": v(485.26, 28.8) * mm});
            skLineSegment(sketch, "E358.MirrorCS", {"start": v(581.76, 29.16) * mm, "end": v(591.58, 29.2) * mm});
            skLineSegment(sketch, "E359.MirrorCS", {"start": v(520.88, 28.94) * mm, "end": v(520.88, 29.7) * mm});
            skLineSegment(sketch, "E360.MirrorCS", {"start": v(319.57, 28.2) * mm, "end": v(319.56, 28.96) * mm});
            skLineSegment(sketch, "E361.MirrorCS", {"start": v(456.03, 28.7) * mm, "end": v(456.03, 29.46) * mm});
            skLineSegment(sketch, "E362.MirrorCS", {"start": v(564.62, 29.86) * mm, "end": v(564.62, 29.1) * mm});
            skLineSegment(sketch, "E363.MirrorCS", {"start": v(385.27, 29.2) * mm, "end": v(385.27, 28.44) * mm});
            skLineSegment(sketch, "E364.MirrorCS", {"start": v(378.92, 28.41) * mm, "end": v(378.92, 29.18) * mm});
            skLineSegment(sketch, "E365.MirrorCS", {"start": v(506.85, 29.65) * mm, "end": v(506.85, 28.89) * mm});
            skLineSegment(sketch, "E366.MirrorCS", {"start": v(597.93, 29.22) * mm, "end": v(606.85, 29.25) * mm});
            skLineSegment(sketch, "E367.MirrorCS", {"start": v(546.46, 29.03) * mm, "end": v(558.27, 29.08) * mm});
            skLineSegment(sketch, "E368.MirrorCS", {"start": v(143.75, 28.31) * mm, "end": v(143.75, 27.55) * mm});
            skLineSegment(sketch, "E369.MirrorCS", {"start": v(137.4, 27.53) * mm, "end": v(137.4, 28.29) * mm});
            skLineSegment(sketch, "E370.MirrorCS", {"start": v(100.57, 28.15) * mm, "end": v(100.57, 27.39) * mm});
            skLineSegment(sketch, "E371.MirrorCS", {"start": v(54.82, 27.98) * mm, "end": v(54.82, 27.22) * mm});
            skLineSegment(sketch, "E372.MirrorCS", {"start": v(6.35, 27.8) * mm, "end": v(6.35, 27.04) * mm});
            skLineSegment(sketch, "E373.MirrorCS", {"start": v(178.15, 27.68) * mm, "end": v(178.15, 28.44) * mm});
            skLineSegment(sketch, "E374.MirrorCS", {"start": v(431.8, 28.6) * mm, "end": v(431.8, 29.37) * mm});
            skLineSegment(sketch, "E375.MirrorCS", {"start": v(546.46, 29.8) * mm, "end": v(546.46, 29.03) * mm});
            skLineSegment(sketch, "E376.MirrorCS", {"start": v(500.5, 28.86) * mm, "end": v(500.5, 29.62) * mm});
            skLineSegment(sketch, "E377.MirrorCS", {"start": v(287.22, 28.08) * mm, "end": v(287.21, 28.84) * mm});
            skLineSegment(sketch, "E378.MirrorCS", {"start": v(564.62, 29.1) * mm, "end": v(575.4, 29.14) * mm});
            skLineSegment(sketch, "E379.MirrorCS", {"start": v(252.94, 27.95) * mm, "end": v(252.94, 28.71) * mm});
            skLineSegment(sketch, "E380.MirrorCS", {"start": v(613.2, 29.28) * mm, "end": v(621.26, 29.3) * mm});
            skLineSegment(sketch, "E381.MirrorCS", {"start": v(527.23, 29.72) * mm, "end": v(527.23, 28.96) * mm});
            skLineSegment(sketch, "E382.MirrorCS", {"start": v(350.1, 28.3) * mm, "end": v(350.1, 29.07) * mm});
            skLineSegment(sketch, "E383.MirrorCS", {"start": v(412.47, 29.3) * mm, "end": v(412.47, 28.54) * mm});
            skLineSegment(sketch, "E384.MirrorCS", {"start": v(575.4, 29.14) * mm, "end": v(575.4, 29.9) * mm});
            skLineSegment(sketch, "E385.MirrorCS", {"start": v(259.3, 28.74) * mm, "end": v(259.3, 27.97) * mm});
            skLineSegment(sketch, "E386.MirrorCS", {"start": v(621.26, 29.3) * mm, "end": v(621.26, 30.07) * mm});
            skLineSegment(sketch, "E387.MirrorCS", {"start": v(356.45, 29.1) * mm, "end": v(356.45, 28.33) * mm});
            skLineSegment(sketch, "E388.MirrorCS", {"start": v(506.85, 28.89) * mm, "end": v(520.88, 28.94) * mm});
            skLineSegment(sketch, "E389.MirrorCS", {"start": v(438.15, 29.4) * mm, "end": v(438.15, 28.63) * mm});
            skLineSegment(sketch, "E390.MirrorCS", {"start": v(184.5, 27.7) * mm, "end": v(216.63, 27.82) * mm, "construction": true});
            skLineSegment(sketch, "E391.MirrorCS", {"start": v(462.38, 29.48) * mm, "end": v(462.38, 28.72) * mm});
            skLineSegment(sketch, "E392.MirrorCS", {"start": v(540.11, 29) * mm, "end": v(540.11, 29.77) * mm});
            skLineSegment(sketch, "E393.MirrorCS", {"start": v(527.23, 28.96) * mm, "end": v(540.11, 29) * mm});
            skLineSegment(sketch, "E394.MirrorCS", {"start": v(222.98, 27.84) * mm, "end": v(252.94, 27.95) * mm});
            skLineSegment(sketch, "E395.MirrorCS", {"start": v(385.27, 28.44) * mm, "end": v(406.12, 28.51) * mm});
            skLineSegment(sketch, "E396.MirrorCS", {"start": v(293.57, 28.1) * mm, "end": v(319.57, 28.2) * mm});
            skLineSegment(sketch, "E397.MirrorCS", {"start": v(438.15, 28.63) * mm, "end": v(456.03, 28.7) * mm});
            skLineSegment(sketch, "E398.MirrorCS", {"start": v(143.75, 27.55) * mm, "end": v(178.15, 27.68) * mm});
            skLineSegment(sketch, "E399.MirrorCS", {"start": v(54.82, 27.22) * mm, "end": v(94.22, 27.37) * mm});
            skLineSegment(sketch, "E400.MirrorCS", {"start": v(6.35, 27.04) * mm, "end": v(48.47, 27.2) * mm});
            skLineSegment(sketch, "E401.MirrorCS", {"start": v(356.45, 28.33) * mm, "end": v(378.92, 28.41) * mm});
            skLineSegment(sketch, "E402.MirrorCS", {"start": v(259.3, 27.97) * mm, "end": v(287.22, 28.08) * mm});
            skLineSegment(sketch, "E403.MirrorCS", {"start": v(485.26, 28.8) * mm, "end": v(500.5, 28.86) * mm});
            skLineSegment(sketch, "E404.MirrorCS", {"start": v(412.47, 28.54) * mm, "end": v(431.8, 28.6) * mm});
            skLineSegment(sketch, "E405.MirrorCS", {"start": v(184.5, 27.7) * mm, "end": v(216.63, 27.82) * mm});
            skLineSegment(sketch, "E406.MirrorCS", {"start": v(462.38, 28.72) * mm, "end": v(478.9, 28.78) * mm});
            skLineSegment(sketch, "E407.MirrorCS", {"start": v(325.92, 28.22) * mm, "end": v(350.1, 28.3) * mm});
            skLineSegment(sketch, "E408.MirrorCS", {"start": v(100.57, 27.39) * mm, "end": v(137.4, 27.53) * mm});
            skLineSegment(sketch, "E409", {"start": v(0, 38.9) * mm, "end": v(646.62, 46.04) * mm, "construction": true});
            skLineSegment(sketch, "E410", {"start": v(0, 39.66) * mm, "end": v(642.93, 46.76) * mm, "construction": true});
            skLineSegment(sketch, "E411", {"start": v(6.35, 38.96) * mm, "end": v(6.34, 39.73) * mm});
            skLineSegment(sketch, "E412", {"start": v(6.34, 39.73) * mm, "end": v(48.46, 40.2) * mm});
            skLineSegment(sketch, "E413", {"start": v(48.46, 40.2) * mm, "end": v(48.47, 39.43) * mm});
            skLineSegment(sketch, "E414", {"start": v(54.82, 39.5) * mm, "end": v(54.8, 40.26) * mm});
            skLineSegment(sketch, "E415", {"start": v(54.8, 40.26) * mm, "end": v(94.2, 40.7) * mm});
            skLineSegment(sketch, "E416", {"start": v(94.2, 40.7) * mm, "end": v(94.21, 39.93) * mm});
            skLineSegment(sketch, "E417", {"start": v(100.56, 40) * mm, "end": v(100.56, 40.77) * mm});
            skLineSegment(sketch, "E418", {"start": v(100.56, 40.77) * mm, "end": v(137.39, 41.17) * mm});
            skLineSegment(sketch, "E419", {"start": v(137.39, 41.17) * mm, "end": v(137.4, 40.41) * mm});
            skLineSegment(sketch, "E420", {"start": v(143.74, 40.48) * mm, "end": v(143.74, 41.24) * mm});
            skLineSegment(sketch, "E421", {"start": v(143.74, 41.24) * mm, "end": v(178.13, 41.62) * mm});
            skLineSegment(sketch, "E422", {"start": v(178.13, 41.62) * mm, "end": v(178.14, 40.86) * mm});
            skLineSegment(sketch, "E423", {"start": v(184.5, 40.93) * mm, "end": v(184.48, 41.7) * mm});
            skLineSegment(sketch, "E424", {"start": v(184.48, 41.7) * mm, "end": v(216.6, 42.05) * mm, "construction": true});
            skLineSegment(sketch, "E425", {"start": v(216.6, 42.05) * mm, "end": v(216.62, 41.29) * mm});
            skLineSegment(sketch, "E426", {"start": v(222.97, 41.36) * mm, "end": v(222.96, 42.12) * mm});
            skLineSegment(sketch, "E427", {"start": v(222.96, 42.12) * mm, "end": v(252.92, 42.45) * mm});
            skLineSegment(sketch, "E428", {"start": v(252.92, 42.45) * mm, "end": v(252.93, 41.69) * mm});
            skLineSegment(sketch, "E429", {"start": v(259.28, 41.76) * mm, "end": v(259.27, 42.52) * mm});
            skLineSegment(sketch, "E430", {"start": v(259.27, 42.52) * mm, "end": v(287.2, 42.83) * mm});
            skLineSegment(sketch, "E431", {"start": v(287.2, 42.83) * mm, "end": v(287.2, 42.07) * mm});
            skLineSegment(sketch, "E432", {"start": v(293.55, 42.14) * mm, "end": v(293.54, 42.9) * mm});
            skLineSegment(sketch, "E433", {"start": v(293.54, 42.9) * mm, "end": v(319.54, 43.19) * mm});
            skLineSegment(sketch, "E434", {"start": v(319.54, 43.19) * mm, "end": v(319.55, 42.42) * mm});
            skLineSegment(sketch, "E435", {"start": v(325.9, 42.5) * mm, "end": v(325.89, 43.26) * mm});
            skLineSegment(sketch, "E436", {"start": v(325.89, 43.26) * mm, "end": v(350.07, 43.52) * mm});
            skLineSegment(sketch, "E437", {"start": v(350.07, 43.52) * mm, "end": v(350.08, 42.76) * mm});
            skLineSegment(sketch, "E438", {"start": v(184.48, 41.7) * mm, "end": v(216.6, 42.05) * mm});
            skLineSegment(sketch, "E439", {"start": v(356.43, 42.83) * mm, "end": v(356.42, 43.6) * mm});
            skLineSegment(sketch, "E440", {"start": v(356.42, 43.6) * mm, "end": v(378.89, 43.84) * mm});
            skLineSegment(sketch, "E441", {"start": v(378.89, 43.84) * mm, "end": v(378.9, 43.08) * mm});
            skLineSegment(sketch, "E442", {"start": v(385.25, 43.15) * mm, "end": v(385.24, 43.91) * mm});
            skLineSegment(sketch, "E443", {"start": v(385.24, 43.91) * mm, "end": v(406.1, 44.14) * mm});
            skLineSegment(sketch, "E444", {"start": v(406.1, 44.14) * mm, "end": v(406.1, 43.38) * mm});
            skLineSegment(sketch, "E445", {"start": v(412.45, 43.45) * mm, "end": v(412.44, 44.21) * mm});
            skLineSegment(sketch, "E446", {"start": v(412.44, 44.21) * mm, "end": v(431.77, 44.43) * mm});
            skLineSegment(sketch, "E447", {"start": v(431.77, 44.43) * mm, "end": v(431.77, 43.66) * mm});
            skLineSegment(sketch, "E448", {"start": v(438.12, 43.73) * mm, "end": v(438.11, 44.5) * mm});
            skLineSegment(sketch, "E449", {"start": v(438.11, 44.5) * mm, "end": v(456, 44.7) * mm});
            skLineSegment(sketch, "E450", {"start": v(456, 44.7) * mm, "end": v(456, 43.93) * mm});
            skLineSegment(sketch, "E451", {"start": v(462.36, 44) * mm, "end": v(462.35, 44.76) * mm});
            skLineSegment(sketch, "E452", {"start": v(462.35, 44.76) * mm, "end": v(478.87, 44.95) * mm});
            skLineSegment(sketch, "E453", {"start": v(478.87, 44.95) * mm, "end": v(478.88, 44.18) * mm});
            skLineSegment(sketch, "E454", {"start": v(485.23, 44.25) * mm, "end": v(485.22, 45.02) * mm});
            skLineSegment(sketch, "E455", {"start": v(485.22, 45.02) * mm, "end": v(500.46, 45.18) * mm});
            skLineSegment(sketch, "E456", {"start": v(500.46, 45.18) * mm, "end": v(500.47, 44.42) * mm});
            skLineSegment(sketch, "E457", {"start": v(506.82, 44.5) * mm, "end": v(506.81, 45.25) * mm});
            skLineSegment(sketch, "E458", {"start": v(506.81, 45.25) * mm, "end": v(520.84, 45.4) * mm});
            skLineSegment(sketch, "E459", {"start": v(520.84, 45.4) * mm, "end": v(520.85, 44.65) * mm});
            skLineSegment(sketch, "E460", {"start": v(527.2, 44.72) * mm, "end": v(527.19, 45.48) * mm});
            skLineSegment(sketch, "E461", {"start": v(527.19, 45.48) * mm, "end": v(540.07, 45.62) * mm});
            skLineSegment(sketch, "E462", {"start": v(540.07, 45.62) * mm, "end": v(540.08, 44.86) * mm});
            skLineSegment(sketch, "E463", {"start": v(546.43, 44.93) * mm, "end": v(546.42, 45.7) * mm});
            skLineSegment(sketch, "E464", {"start": v(546.42, 45.7) * mm, "end": v(558.23, 45.82) * mm});
            skLineSegment(sketch, "E465", {"start": v(558.23, 45.82) * mm, "end": v(558.24, 45.06) * mm});
            skLineSegment(sketch, "E466", {"start": v(564.59, 45.13) * mm, "end": v(564.58, 45.9) * mm});
            skLineSegment(sketch, "E467", {"start": v(564.58, 45.9) * mm, "end": v(575.36, 46.01) * mm});
            skLineSegment(sketch, "E468", {"start": v(575.36, 46.01) * mm, "end": v(575.37, 45.25) * mm});
            skLineSegment(sketch, "E469", {"start": v(581.72, 45.32) * mm, "end": v(581.71, 46.08) * mm});
            skLineSegment(sketch, "E470", {"start": v(581.71, 46.08) * mm, "end": v(591.54, 46.2) * mm});
            skLineSegment(sketch, "E471", {"start": v(591.54, 46.2) * mm, "end": v(591.55, 45.43) * mm});
            skLineSegment(sketch, "E472", {"start": v(597.9, 45.5) * mm, "end": v(597.89, 46.26) * mm});
            skLineSegment(sketch, "E473", {"start": v(597.89, 46.26) * mm, "end": v(606.8, 46.36) * mm});
            skLineSegment(sketch, "E474", {"start": v(606.8, 46.36) * mm, "end": v(606.81, 45.6) * mm});
            skLineSegment(sketch, "E475", {"start": v(613.16, 45.67) * mm, "end": v(613.15, 46.43) * mm});
            skLineSegment(sketch, "E476", {"start": v(613.15, 46.43) * mm, "end": v(621.21, 46.52) * mm});
            skLineSegment(sketch, "E477", {"start": v(621.21, 46.52) * mm, "end": v(621.22, 45.76) * mm});
            skLineSegment(sketch, "E478.MirrorCS", {"start": v(184.5, 40.93) * mm, "end": v(184.5, 40.17) * mm});
            skLineSegment(sketch, "E479.MirrorCS", {"start": v(606.82, 44.84) * mm, "end": v(606.81, 45.6) * mm});
            skLineSegment(sketch, "E480.MirrorCS", {"start": v(222.97, 41.36) * mm, "end": v(222.98, 40.6) * mm});
            skLineSegment(sketch, "E481.MirrorCS", {"start": v(558.25, 44.3) * mm, "end": v(558.24, 45.06) * mm});
            skLineSegment(sketch, "E482.MirrorCS", {"start": v(216.63, 40.52) * mm, "end": v(216.62, 41.29) * mm});
            skLineSegment(sketch, "E483.MirrorCS", {"start": v(293.55, 42.14) * mm, "end": v(293.56, 41.37) * mm});
            skLineSegment(sketch, "E484.MirrorCS", {"start": v(94.22, 39.17) * mm, "end": v(94.21, 39.93) * mm});
            skLineSegment(sketch, "E485.MirrorCS", {"start": v(48.48, 38.67) * mm, "end": v(48.47, 39.43) * mm});
            skLineSegment(sketch, "E486.MirrorCS", {"start": v(613.16, 45.67) * mm, "end": v(613.17, 44.9) * mm});
            skLineSegment(sketch, "E487.MirrorCS", {"start": v(597.9, 45.5) * mm, "end": v(597.9, 44.74) * mm});
            skLineSegment(sketch, "E488.MirrorCS", {"start": v(325.9, 42.5) * mm, "end": v(325.9, 41.73) * mm});
            skLineSegment(sketch, "E489.MirrorCS", {"start": v(581.72, 45.32) * mm, "end": v(581.73, 44.56) * mm});
            skLineSegment(sketch, "E490.MirrorCS", {"start": v(478.89, 43.42) * mm, "end": v(478.88, 44.18) * mm});
            skLineSegment(sketch, "E491.MirrorCS", {"start": v(406.1, 42.62) * mm, "end": v(406.1, 43.38) * mm});
            skLineSegment(sketch, "E492.MirrorCS", {"start": v(591.56, 44.67) * mm, "end": v(591.55, 45.43) * mm});
            skLineSegment(sketch, "E493.MirrorCS", {"start": v(485.23, 44.25) * mm, "end": v(485.24, 43.5) * mm});
            skLineSegment(sketch, "E494.MirrorCS", {"start": v(581.73, 44.56) * mm, "end": v(591.56, 44.67) * mm});
            skLineSegment(sketch, "E495.MirrorCS", {"start": v(520.86, 43.89) * mm, "end": v(520.85, 44.65) * mm});
            skLineSegment(sketch, "E496.MirrorCS", {"start": v(319.55, 41.66) * mm, "end": v(319.55, 42.42) * mm});
            skLineSegment(sketch, "E497.MirrorCS", {"start": v(456.02, 43.17) * mm, "end": v(456, 43.93) * mm});
            skLineSegment(sketch, "E498.MirrorCS", {"start": v(564.59, 45.13) * mm, "end": v(564.6, 44.37) * mm});
            skLineSegment(sketch, "E499.MirrorCS", {"start": v(385.25, 43.15) * mm, "end": v(385.26, 42.39) * mm});
            skLineSegment(sketch, "E500.MirrorCS", {"start": v(378.9, 42.32) * mm, "end": v(378.9, 43.08) * mm});
            skLineSegment(sketch, "E501.MirrorCS", {"start": v(506.82, 44.5) * mm, "end": v(506.83, 43.73) * mm});
            skLineSegment(sketch, "E502.MirrorCS", {"start": v(597.9, 44.74) * mm, "end": v(606.82, 44.84) * mm});
            skLineSegment(sketch, "E503.MirrorCS", {"start": v(546.44, 44.17) * mm, "end": v(558.25, 44.3) * mm});
            skLineSegment(sketch, "E504.MirrorCS", {"start": v(143.74, 40.48) * mm, "end": v(143.75, 39.72) * mm});
            skLineSegment(sketch, "E505.MirrorCS", {"start": v(137.4, 39.65) * mm, "end": v(137.4, 40.41) * mm});
            skLineSegment(sketch, "E506.MirrorCS", {"start": v(100.56, 40) * mm, "end": v(100.57, 39.24) * mm});
            skLineSegment(sketch, "E507.MirrorCS", {"start": v(54.82, 39.5) * mm, "end": v(54.83, 38.74) * mm});
            skLineSegment(sketch, "E508.MirrorCS", {"start": v(6.35, 38.96) * mm, "end": v(6.36, 38.2) * mm});
            skLineSegment(sketch, "E509.MirrorCS", {"start": v(178.15, 40.1) * mm, "end": v(178.14, 40.86) * mm});
            skLineSegment(sketch, "E510.MirrorCS", {"start": v(431.78, 42.9) * mm, "end": v(431.77, 43.66) * mm});
            skLineSegment(sketch, "E511.MirrorCS", {"start": v(546.43, 44.93) * mm, "end": v(546.44, 44.17) * mm});
            skLineSegment(sketch, "E512.MirrorCS", {"start": v(500.48, 43.66) * mm, "end": v(500.47, 44.42) * mm});
            skLineSegment(sketch, "E513.MirrorCS", {"start": v(287.2, 41.3) * mm, "end": v(287.2, 42.07) * mm});
            skLineSegment(sketch, "E514.MirrorCS", {"start": v(564.6, 44.37) * mm, "end": v(575.38, 44.49) * mm});
            skLineSegment(sketch, "E515.MirrorCS", {"start": v(252.94, 40.93) * mm, "end": v(252.93, 41.69) * mm});
            skLineSegment(sketch, "E516.MirrorCS", {"start": v(613.17, 44.9) * mm, "end": v(621.23, 45) * mm});
            skLineSegment(sketch, "E517.MirrorCS", {"start": v(527.2, 44.72) * mm, "end": v(527.2, 43.96) * mm});
            skLineSegment(sketch, "E518.MirrorCS", {"start": v(350.09, 42) * mm, "end": v(350.08, 42.76) * mm});
            skLineSegment(sketch, "E519.MirrorCS", {"start": v(412.45, 43.45) * mm, "end": v(412.46, 42.69) * mm});
            skLineSegment(sketch, "E520.MirrorCS", {"start": v(575.38, 44.49) * mm, "end": v(575.37, 45.25) * mm});
            skLineSegment(sketch, "E521.MirrorCS", {"start": v(259.28, 41.76) * mm, "end": v(259.28, 41) * mm});
            skLineSegment(sketch, "E522.MirrorCS", {"start": v(621.23, 45) * mm, "end": v(621.22, 45.76) * mm});
            skLineSegment(sketch, "E523.MirrorCS", {"start": v(356.43, 42.83) * mm, "end": v(356.44, 42.07) * mm});
            skLineSegment(sketch, "E524.MirrorCS", {"start": v(506.83, 43.73) * mm, "end": v(520.86, 43.89) * mm});
            skLineSegment(sketch, "E525.MirrorCS", {"start": v(438.12, 43.73) * mm, "end": v(438.13, 42.97) * mm});
            skLineSegment(sketch, "E526.MirrorCS", {"start": v(184.5, 40.17) * mm, "end": v(216.63, 40.52) * mm, "construction": true});
            skLineSegment(sketch, "E527.MirrorCS", {"start": v(462.36, 44) * mm, "end": v(462.37, 43.24) * mm});
            skLineSegment(sketch, "E528.MirrorCS", {"start": v(540.1, 44.1) * mm, "end": v(540.08, 44.86) * mm});
            skLineSegment(sketch, "E529.MirrorCS", {"start": v(527.2, 43.96) * mm, "end": v(540.1, 44.1) * mm});
            skLineSegment(sketch, "E530.MirrorCS", {"start": v(222.98, 40.6) * mm, "end": v(252.94, 40.93) * mm});
            skLineSegment(sketch, "E531.MirrorCS", {"start": v(385.26, 42.39) * mm, "end": v(406.1, 42.62) * mm});
            skLineSegment(sketch, "E532.MirrorCS", {"start": v(293.56, 41.37) * mm, "end": v(319.55, 41.66) * mm});
            skLineSegment(sketch, "E533.MirrorCS", {"start": v(438.13, 42.97) * mm, "end": v(456.02, 43.17) * mm});
            skLineSegment(sketch, "E534.MirrorCS", {"start": v(143.75, 39.72) * mm, "end": v(178.15, 40.1) * mm});
            skLineSegment(sketch, "E535.MirrorCS", {"start": v(54.83, 38.74) * mm, "end": v(94.22, 39.17) * mm});
            skLineSegment(sketch, "E536.MirrorCS", {"start": v(6.36, 38.2) * mm, "end": v(48.48, 38.67) * mm});
            skLineSegment(sketch, "E537.MirrorCS", {"start": v(356.44, 42.07) * mm, "end": v(378.9, 42.32) * mm});
            skLineSegment(sketch, "E538.MirrorCS", {"start": v(259.28, 41) * mm, "end": v(287.2, 41.3) * mm});
            skLineSegment(sketch, "E539.MirrorCS", {"start": v(485.24, 43.5) * mm, "end": v(500.48, 43.66) * mm});
            skLineSegment(sketch, "E540.MirrorCS", {"start": v(412.46, 42.69) * mm, "end": v(431.78, 42.9) * mm});
            skLineSegment(sketch, "E541.MirrorCS", {"start": v(184.5, 40.17) * mm, "end": v(216.63, 40.52) * mm});
            skLineSegment(sketch, "E542.MirrorCS", {"start": v(462.37, 43.24) * mm, "end": v(478.89, 43.42) * mm});
            skLineSegment(sketch, "E543.MirrorCS", {"start": v(325.9, 41.73) * mm, "end": v(350.09, 42) * mm});
            skLineSegment(sketch, "E544.MirrorCS", {"start": v(100.57, 39.24) * mm, "end": v(137.4, 39.65) * mm});
            skLineSegment(sketch, "E545", {"start": v(0, 22.23) * mm, "end": v(665.02, 22.23) * mm, "construction": true});
            skLineSegment(sketch, "E546.MirrorCS", {"start": v(-33.04, 44.45) * mm, "end": v(118.54, 44.45) * mm, "construction": true});
            skLineSegment(sketch, "E547.MirrorCS", {"start": v(0, 27.02) * mm, "end": v(642.97, 29.39) * mm, "construction": true});
            skLineSegment(sketch, "E548.MirrorCS", {"start": v(0, 38.13) * mm, "end": v(642.95, 45.23) * mm, "construction": true});
            skLineSegment(sketch, "E549.MirrorCS", {"start": v(0, 15.9) * mm, "end": v(642.97, 13.54) * mm, "construction": true});
            skLineSegment(sketch, "E550.MirrorCS", {"start": v(0, 4.8) * mm, "end": v(642.93, -2.3) * mm, "construction": true});
            skSolve(sketch);
        }
        {
            var Q0;
            Q0=qCreatedBy(makeId("Front.planeOp"),FACE);
            var sketch = newSketch(context, id + "F1", { "sketchPlane" : qUnion([Q0])});
            skLineSegment(sketch, "E551", {"start": v(0, 0) * mm, "end": v(0, 44.45) * mm});
            skLineSegment(sketch, "E552", {"start": v(0, 44.45) * mm, "end": v(635, 53.98) * mm});
            skLineSegment(sketch, "E553", {"start": v(635, 53.98) * mm, "end": v(635, -9.53) * mm});
            skLineSegment(sketch, "E554", {"start": v(635, -9.52) * mm, "end": v(0, 0) * mm});
            skLineSegment(sketch, "E555", {"start": v(0, 22.23) * mm, "end": v(897.35, 22.23) * mm, "construction": true});
            skSolve(sketch);
        }
        {
            var Q0;
            Q0=qSketchRegion(id+"F1",true);
            extrude(context, id + "F2", {"entities" : qUnion([Q0]), "depth" : 1.52 * mm});
        }
        {
            var Q0;
            Q0=makeQuery(id+"F2.opExtrude","CAP_FACE",FACE,{"disambiguationData":[OSD([sQuery(id+"F1.wireOp",EDGE,"E551"),sQuery(id+"F1.wireOp",EDGE,"E552"),sQuery(id+"F1.wireOp",EDGE,"E553"),sQuery(id+"F1.wireOp",EDGE,"E554")])],"isStart":false});
            var sketch = newSketch(context, id + "F3", { "sketchPlane" : qUnion([Q0])});
            skLineSegment(sketch, "E556", {"start": v(0, 22.22) * mm, "end": v(635, 22.22) * mm, "construction": true});
            skSolve(sketch);
        }
        {
            var Q0;
            Q0=qSketchRegion(id+"F0",true);
            extrude(context, id + "F4", {"entities" : qUnion([Q0]), "operationType" : NewBodyOperationType.REMOVE, "endBound" : BoundingType.THROUGH_ALL, "depth" : 25.4 * mm});
        }
        {
            var Q0;
            Q0=makeQuery(id+"F3.imprint","IMPRINT",FACE,{"disambiguationData":[TD([[makeQuery(id+"F3.imprint","IMPRINT",EDGE,{"derivedFrom":makeQuery(id+"F2.opExtrude","CAP_EDGE",EDGE,{"disambiguationData":[OSD([sQuery(id+"F1.wireOp",EDGE,"E551")])],"isStart":false})}),-1.0]])]});
            var sketch = newSketch(context, id + "F5", { "sketchPlane" : qUnion([Q0])});
            skCircle(sketch, "E557", {"center": v(97.4, 22.22) * mm, "radius": 1.13 * mm});
            skLineSegment(sketch, "E558", {"start": v(0, 22.22) * mm, "end": v(635, 22.22) * mm, "construction": true});
            skCircle(sketch, "E559", {"center": v(3.18, 22.22) * mm, "radius": 1.13 * mm});
            skCircle(sketch, "E560", {"center": v(181.33, 22.22) * mm, "radius": 1.13 * mm});
            skCircle(sketch, "E561", {"center": v(290.4, 22.22) * mm, "radius": 1.13 * mm});
            skCircle(sketch, "E562", {"center": v(409.3, 22.22) * mm, "radius": 1.13 * mm});
            skCircle(sketch, "E563", {"center": v(524.06, 22.22) * mm, "radius": 1.13 * mm});
            skCircle(sketch, "E564", {"center": v(624.44, 22.22) * mm, "radius": 1.13 * mm});
            skSolve(sketch);
        }
        {
            var Q0;
            Q0=qSketchRegion(id+"F5",true);
            extrude(context, id + "F6", {"entities" : qUnion([Q0]), "operationType" : NewBodyOperationType.REMOVE, "endBound" : BoundingType.THROUGH_ALL, "depth" : 25.4 * mm});
        }
        {
            var Q0;
            Q0=qSketchRegion(id+"F5",true);
            extrude(context, id + "F7", {"entities" : qUnion([Q0]), "operationType" : NewBodyOperationType.REMOVE, "endBound" : BoundingType.THROUGH_ALL, "oppositeDirection" : true, "depth" : 25.4 * mm});
        }
    });
